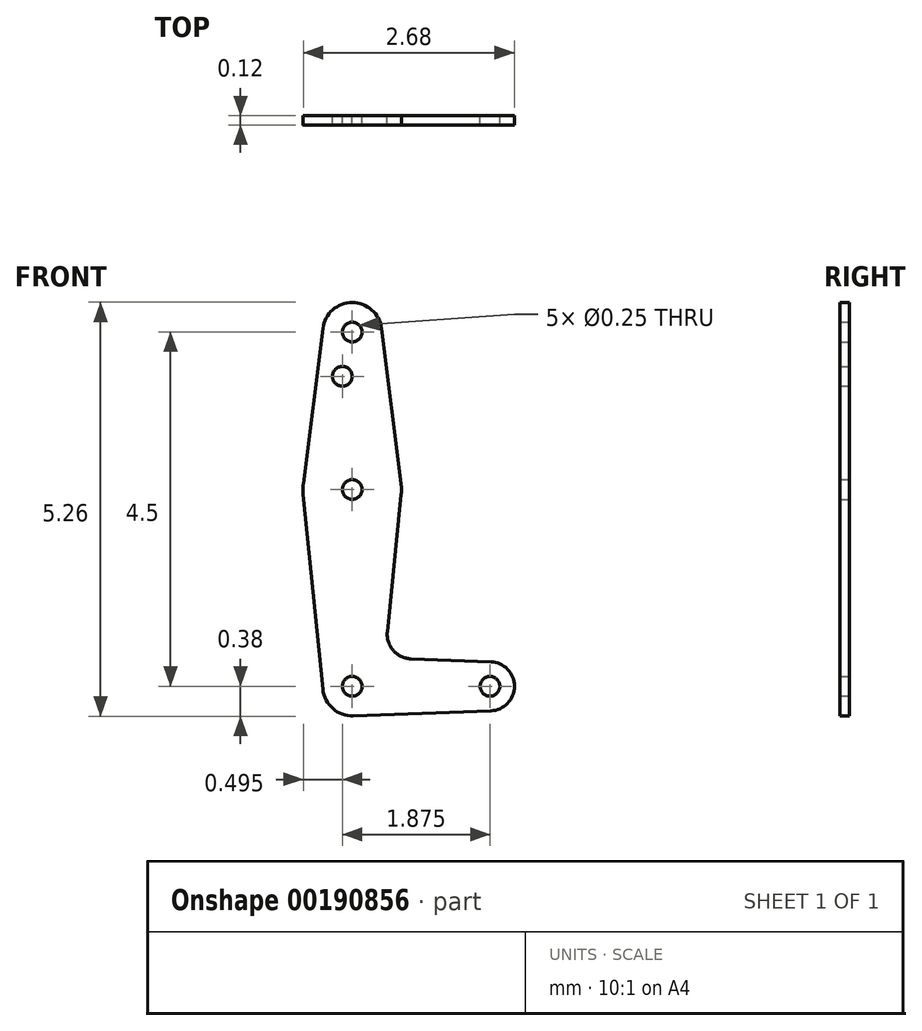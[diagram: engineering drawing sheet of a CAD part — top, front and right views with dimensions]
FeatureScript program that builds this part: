
annotation { "Feature Type Name" : "Feature", "Feature Type Description" : "" }
export const myFeature = defineFeature(function(context is Context, id is Id, definition is map)
    precondition{}
    {
        {
            var Q0;
            Q0=qCreatedBy(makeId("Front.planeOp"),FACE);
            var sketch = newSketch(context, id + "F0", { "sketchPlane" : qUnion([Q0])});
            skLineSegment(sketch, "E0", {"start": v(0, 0) * mm, "end": v(0, 4.5) * mm, "construction": true});
            skLineSegment(sketch, "E1", {"start": v(0, 0) * mm, "end": v(1.75, 0) * mm, "construction": true});
            skCircle(sketch, "E2", {"center": v(0, 4.5) * mm, "radius": 0.38 * mm});
            skCircle(sketch, "E3", {"center": v(0, 2.5) * mm, "radius": 0.62 * mm});
            skCircle(sketch, "E4", {"center": v(0, 0) * mm, "radius": 0.38 * mm});
            skCircle(sketch, "E5", {"center": v(1.75, 0) * mm, "radius": 0.31 * mm});
            skLineSegment(sketch, "E6", {"start": v(-0.37, 4.55) * mm, "end": v(-0.62, 2.58) * mm});
            skLineSegment(sketch, "E7", {"start": v(0.37, 4.55) * mm, "end": v(0.62, 2.58) * mm});
            skLineSegment(sketch, "E8", {"start": v(-0.37, -0.04) * mm, "end": v(-0.62, 2.44) * mm});
            skLineSegment(sketch, "E9", {"start": v(0.62, 2.44) * mm, "end": v(0.45, 0.7) * mm});
            skLineSegment(sketch, "E10", {"start": v(0.75, 0.35) * mm, "end": v(1.76, 0.31) * mm});
            skLineSegment(sketch, "E11", {"start": v(0.01, -0.37) * mm, "end": v(1.76, -0.31) * mm});
            skCircle(sketch, "E12", {"center": v(0, 4.5) * mm, "radius": 0.12 * mm});
            skCircle(sketch, "E13", {"center": v(0, 2.5) * mm, "radius": 0.12 * mm});
            skCircle(sketch, "E14", {"center": v(0, 0) * mm, "radius": 0.12 * mm});
            skCircle(sketch, "E15", {"center": v(1.75, 0) * mm, "radius": 0.12 * mm});
            skCircle(sketch, "E16", {"center": v(-0.13, 3.94) * mm, "radius": 0.12 * mm});
            skArc(sketch, "E17.filletArc", {"start": v(0.45, 0.7) * mm, "mid": v(0.52, 0.46) * mm, "end": v(0.75, 0.35) * mm});
            skSolve(sketch);
        }
        {
            var Q0;
            Q0 = qSketchRegion(id + "F0", true);
            extrude(context, id + "F1", {"entities" : qUnion([Q0]), "depth" : .12 * mm});
        }
    });
